FCSTD DOCUMENT  (FreeCAD 0.20R26155 (Git))
Label: JST-XH-edgemount-2p
License: All rights reserved
LicenseURL: http://en.wikipedia.org/wiki/All_rights_reserved
objects: Sketcher::SketchObject×2, PartDesign::Body×1
note: 3 computed .brp shape members not serialized (recipe doc carries the construction recipe); baked Part::Feature solids carry a one-line shape summary decoded from their .brp

FEATURE [Sketcher::SketchObject] Sketch  label="Pads_TH_SMD"
  FullyConstrained = false
  MapMode = 5
  Support = -> [XY_Plane]
  sketch-geometry (10):
    g0: LineSegment StartX=-2.72969 StartY=1.75 StartZ=0 EndX=-1.22969 EndY=1.75 EndZ=0
    g1: LineSegment StartX=-1.22969 StartY=1.75 StartZ=0 EndX=-1.22969 EndY=-1.75 EndZ=0
    g2: LineSegment StartX=-1.22969 StartY=-1.75 StartZ=0 EndX=-2.72969 EndY=-1.75 EndZ=0
    g3: LineSegment StartX=-2.72969 StartY=-1.75 StartZ=0 EndX=-2.72969 EndY=1.75 EndZ=0
    g4: LineSegment StartX=-0.229693 StartY=1.75 StartZ=0 EndX=1.27031 EndY=1.75 EndZ=0
    g5: LineSegment StartX=1.27031 StartY=1.75 StartZ=0 EndX=1.27031 EndY=-1.75 EndZ=0
    g6: LineSegment StartX=1.27031 StartY=-1.75 StartZ=0 EndX=-0.229693 EndY=-1.75 EndZ=0
    g7: LineSegment StartX=-0.229693 StartY=-1.75 StartZ=0 EndX=-0.229693 EndY=1.75 EndZ=0
    g8: GeomPoint X=-1.97969 Y=1.75 Z=0
    g9: GeomPoint X=0.520307 Y=1.75 Z=0
  constraints (23):
    c: Coincident(g0,g1)
    c: Coincident(g1,g2)
    c: Coincident(g2,g3)
    c: Coincident(g3,g0)
    c: Horizontal(g0)
    c: Horizontal(g2)
    c: Vertical(g3)
    c: Coincident(g4,g5)
    c: Coincident(g5,g6)
    c: Coincident(g6,g7)
    c: Coincident(g7,g4)
    c: Horizontal(g4)
    c: Horizontal(g6)
    c: Vertical(g7)
    c: Symmetric(g4,g5,g-1)
    c: Symmetric(g0,g1,g-1)
    c: Equal(g1,g7)
    c: DistanceY(g3,g3) = 3.5
    c: Equal(g0,g4)
    c: DistanceX(g0,g0) = 1.5
    c: Symmetric(g4,g4,g9)
    c: Symmetric(g0,g0,g8)
    c: DistanceX(g8,g9) = 2.5
FEATURE [Sketcher::SketchObject] Sketch001  label="F_CrtYd_0.05"
  ExternalGeometry = -> [Sketch]
  FullyConstrained = true
  MapMode = 5
  Support = -> [XY_Plane]
  sketch-geometry (8):
    g0: GeomPoint X=-0.729693 Y=2.75 Z=0
    g1: LineSegment StartX=-4.42969 StartY=9.75 StartZ=0 EndX=2.97031 EndY=9.75 EndZ=0
    g2: LineSegment StartX=2.97031 StartY=9.75 StartZ=0 EndX=2.97031 EndY=2.75 EndZ=0
    g3: LineSegment StartX=2.97031 StartY=2.75 StartZ=0 EndX=-4.42969 EndY=2.75 EndZ=0
    g4: LineSegment StartX=-4.42969 StartY=2.75 StartZ=0 EndX=-4.42969 EndY=9.75 EndZ=0
    g5: LineSegment StartX=-2.72969 StartY=1.75 StartZ=0 EndX=1.27031 EndY=1.75 EndZ=0
    g6: GeomPoint X=-0.729693 Y=1.75 Z=0
    g7: LineSegment StartX=-0.729693 StartY=1.75 StartZ=0 EndX=-0.729693 EndY=2.75 EndZ=0
  constraints (18):
    c: Coincident(g1,g2)
    c: Coincident(g2,g3)
    c: Coincident(g3,g4)
    c: Coincident(g4,g1)
    c: Horizontal(g1)
    c: Horizontal(g3)
    c: Vertical(g2)
    c: Vertical(g4)
    c: Symmetric(g3,g3,g0)
    c: DistanceX(g3,g3) = 7.4
    c: DistanceY(g4,g4) = 7
    c: Coincident(g5,g-3)
    c: Coincident(g5,g-4)
    c: Symmetric(g5,g5,g6)
    c: Coincident(g7,g6)
    c: Coincident(g7,g0)
    c: Vertical(g7)
    c: DistanceY(g7,g7) = 1
FEATURE [PartDesign::Body] Body  label="JST-XH-edgemount"
  Group = -> [Sketch,Sketch001]
  Origin = -> Origin
